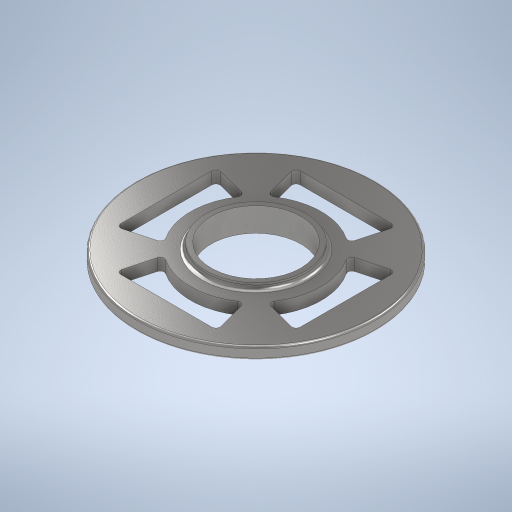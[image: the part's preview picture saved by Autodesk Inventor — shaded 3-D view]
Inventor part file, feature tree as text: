
AUTODESK INVENTOR PART (.ipt)
format: ipt  version: 2024 (Build 280153000, 153)  size: 376,320 bytes
history: native  units: mm
features: fillet x5, extrude x4, sketch x4, plane x1, pattern_circular x1
ambient origin geometry x8: Origin, YZ Plane, XZ Plane, XY Plane, X Axis, Y Axis, Z Axis, Center Point
bodies: Volumenkörper1 (feature_tree)
feature tree (15):
  extrude  "Extrusion1"  Depth=6.0mm TaperAngle=0.0deg
  plane  "Arbeitsebene1"
  extrude  "Extrusion2"  Depth=3.0mm
  extrude  "Extrusion3"  Depth=2.0mm
  fillet  "Rundung1"  Radius=12.0mm
  fillet  "Rundung2"  Radius=2.0mm
  extrude  "Extrusion4"  Depth=1.0mm
  fillet  "Rundung3"  Radius=45.0mm
  fillet  "Rundung4"  [1 undecoded]
  pattern_circular  "Runde Anordnung1"  [2 undecoded]
  fillet  "Rundung5"  Radius=2.0mm
  sketch  "Skizze1"  dims[d0=120.0mm d1=6.0mm d2=0.0mm]
  sketch  "Skizze3"  dims[d4=3.0mm d5=50.0mm]
  sketch  "Skizze4"  dims[d6=12.0mm d7=0.0mm d8=45.0mm d9=12.0mm d10=0.0mm d11=2.0mm]
  sketch  "Skizze5"  dims[d12=2.0mm d16=20.0mm d17=45.0mm d18=75.0deg d19=12.0mm d20=0.0mm d21=2.0mm d22=2.0mm d23=40.0mm d24=360.0deg d26=1.0mm]
note: 3 required parameter values undecoded (feature->parameter linkage not recoverable at this tier; creation-order binding heuristic only, values carry confidence <= 0.55)
